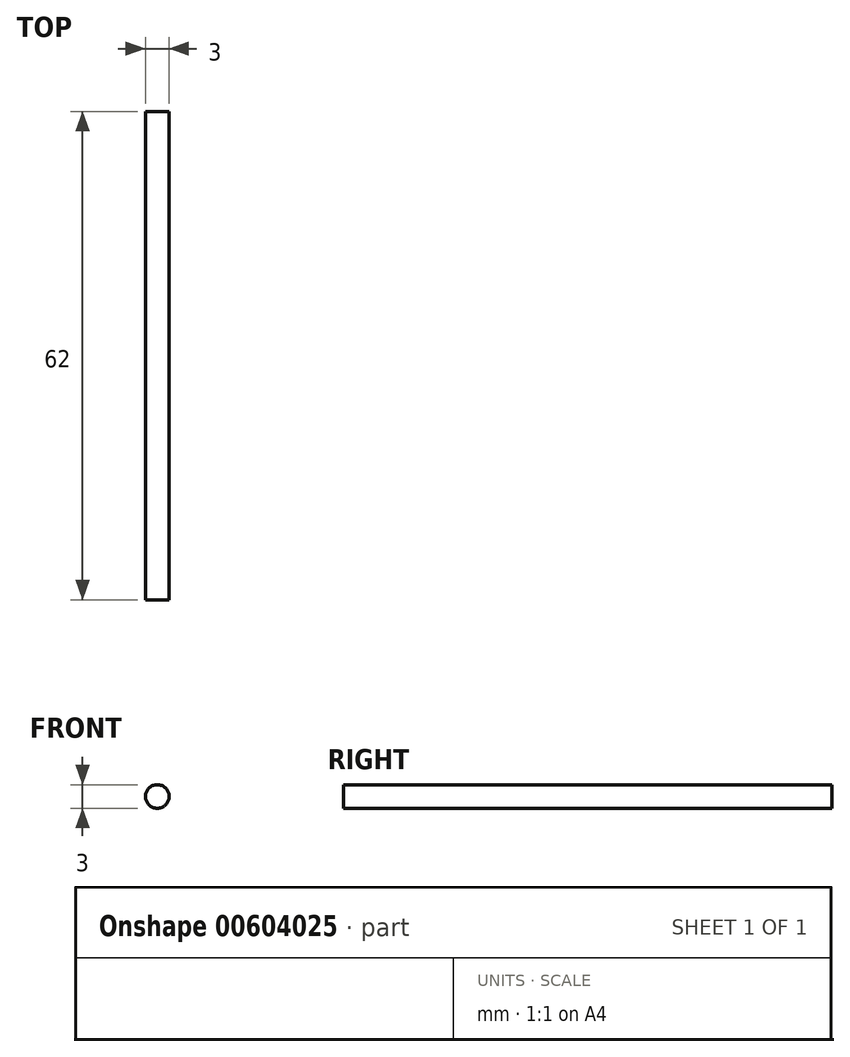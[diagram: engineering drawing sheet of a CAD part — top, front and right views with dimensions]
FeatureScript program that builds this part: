
annotation { "Feature Type Name" : "Feature", "Feature Type Description" : "" }
export const myFeature = defineFeature(function(context is Context, id is Id, definition is map)
    precondition{}
    {
        {
            var Q0;
            Q0=qCreatedBy(makeId("Front.planeOp"),FACE);
            var sketch = newSketch(context, id + "F0", { "sketchPlane" : qUnion([Q0])});
            skCircle(sketch, "E0", {"center": v(-41.93, 21.97) * mm, "radius": 1.5 * mm});
            skSolve(sketch);
        }
        {
            var Q0;
            Q0=makeQuery(id+"F0.imprint","IMPRINT",FACE,{"disambiguationData":[TD([[makeQuery(id+"F0.imprint","IMPRINT",EDGE,{"derivedFrom":sQuery(id+"F0.wireOp",EDGE,"E0")}),1.0]])]});
            extrude(context, id + "F1", {"entities" : qUnion([Q0]), "endBound" : BoundingType.SYMMETRIC, "depth" : 62 * mm, "offsetDistance" : 25 * mm});
        }
    });
